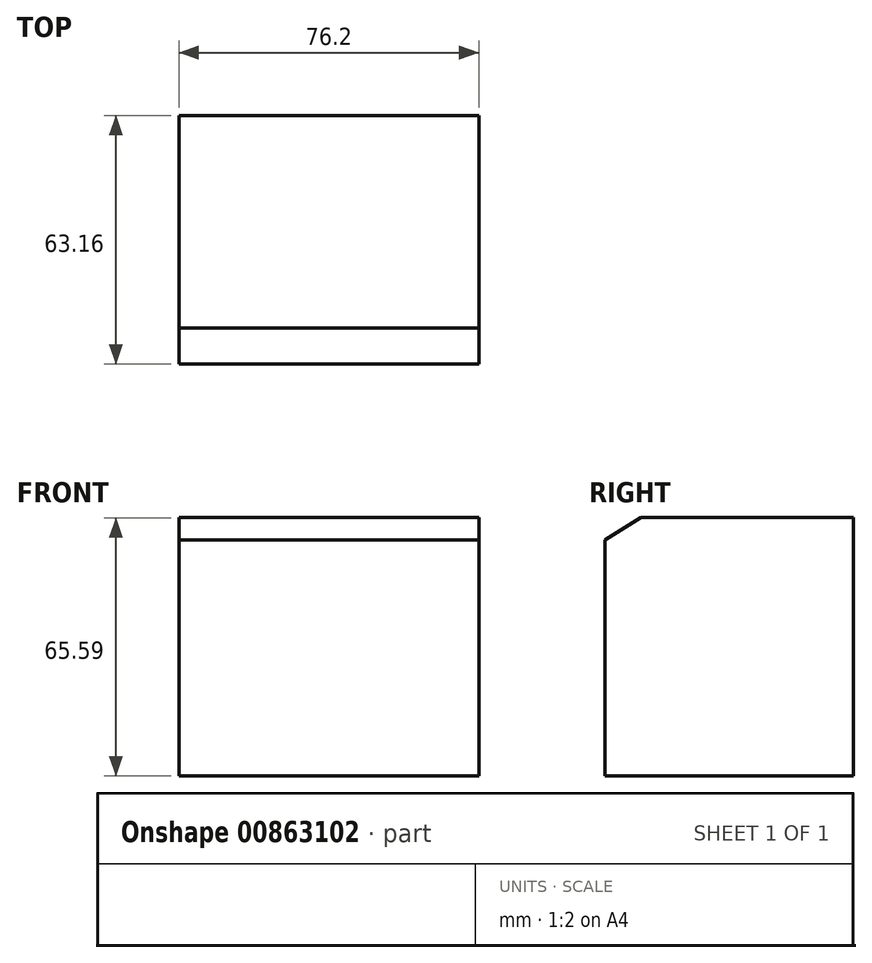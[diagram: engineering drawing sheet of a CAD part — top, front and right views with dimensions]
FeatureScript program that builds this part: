
annotation { "Feature Type Name" : "Feature", "Feature Type Description" : "" }
export const myFeature = defineFeature(function(context is Context, id is Id, definition is map)
    precondition{}
    {
        {
            var Q0;
            Q0=qCreatedBy(makeId("Right.planeOp"),FACE);
            var sketch = newSketch(context, id + "F0", { "sketchPlane" : qUnion([Q0])});
            skLineSegment(sketch, "E0", {"start": v(28.13, -4.57) * mm, "end": v(28.13, 61.02) * mm});
            skLineSegment(sketch, "E1", {"start": v(28.13, 61.02) * mm, "end": v(-15.74, 61.02) * mm});
            skLineSegment(sketch, "E2", {"start": v(-15.74, 61.02) * mm, "end": v(-25.9, 61.02) * mm});
            skLineSegment(sketch, "E3", {"start": v(-25.9, 61.02) * mm, "end": v(-35.03, 55.34) * mm});
            skLineSegment(sketch, "E4", {"start": v(28.13, -4.57) * mm, "end": v(-35.03, -4.57) * mm});
            skLineSegment(sketch, "E5", {"start": v(-35.03, 55.34) * mm, "end": v(-35.03, -4.57) * mm});
            skSolve(sketch);
        }
        {
            var Q0;
            Q0=makeQuery(id+"F0.imprint","IMPRINT",FACE,{"disambiguationData":[TD([[makeQuery(id+"F0.imprint","IMPRINT",EDGE,{"derivedFrom":sQuery(id+"F0.wireOp",EDGE,"E0")}),1.0]])]});
            extrude(context, id + "F1", {"entities" : qUnion([Q0]), "depth" : 76.2 * mm, "offsetDistance" : 25.4 * mm});
        }
    });
